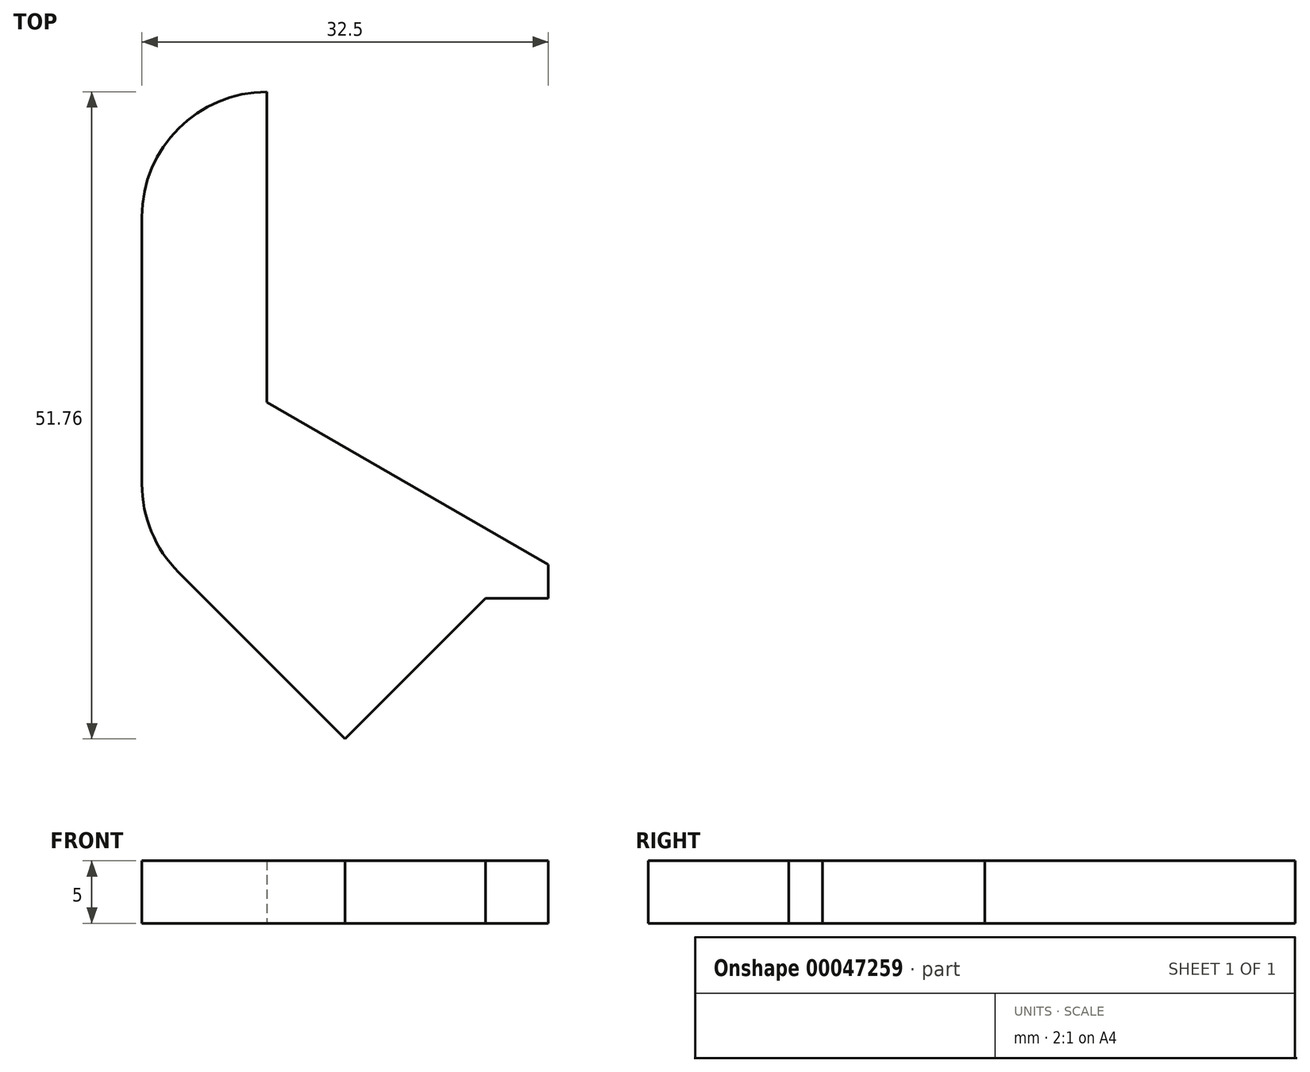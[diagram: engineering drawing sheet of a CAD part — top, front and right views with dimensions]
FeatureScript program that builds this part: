
annotation { "Feature Type Name" : "Feature", "Feature Type Description" : "" }
export const myFeature = defineFeature(function(context is Context, id is Id, definition is map)
    precondition{}
    {
        {
            var Q0;
            Q0=qCreatedBy(makeId("Top.planeOp"),FACE);
            var sketch = newSketch(context, id + "F0", { "sketchPlane" : qUnion([Q0])});
            skCircle(sketch, "E0.cCircle", {"center": v(0, 0) * mm, "radius": 22.5 * mm, "construction": true});
            skLineSegment(sketch, "E0.2", {"start": v(0, -25.98) * mm, "end": v(-22.5, -13) * mm});
            skLineSegment(sketch, "E0.3", {"start": v(-22.5, -13) * mm, "end": v(-22.5, 11.84) * mm});
            skPoint(sketch, "E0.0.midPoint", {"position": v(22.5, 0) * mm});
            skLineSegment(sketch, "E1", {"start": v(-22.5, 11.84) * mm, "end": v(-32.5, 11.84) * mm});
            skLineSegment(sketch, "E2", {"start": v(0, -28.67) * mm, "end": v(-5, -28.67) * mm});
            skLineSegment(sketch, "E3", {"start": v(-5, -28.67) * mm, "end": v(-5, -38.67) * mm});
            skLineSegment(sketch, "E4", {"start": v(-5, -38.67) * mm, "end": v(0, -38.67) * mm});
            skPoint(sketch, "E5.endSnap0", {"position": v(-2, -38.67) * mm});
            skLineSegment(sketch, "E6", {"start": v(-32.5, 11.84) * mm, "end": v(-32.5, -43.67) * mm});
            skPoint(sketch, "E7.MirrorP", {"position": v(0, -38.67) * mm});
            skLineSegment(sketch, "E8.MirrorCS", {"start": v(0, -28.67) * mm, "end": v(5, -28.67) * mm});
            skLineSegment(sketch, "E9.MirrorCS", {"start": v(5, -28.67) * mm, "end": v(5, -38.67) * mm});
            skLineSegment(sketch, "E10.MirrorCS", {"start": v(5, -38.67) * mm, "end": v(0, -38.67) * mm});
            skLineSegment(sketch, "E11", {"start": v(-32.5, -43.67) * mm, "end": v(0, -43.67) * mm});
            skLineSegment(sketch, "E12", {"start": v(0, -43.67) * mm, "end": v(0, -25.98) * mm});
            skLineSegment(sketch, "E13.MirrorCS", {"start": v(22.5, 11.84) * mm, "end": v(32.5, 11.84) * mm});
            skPoint(sketch, "E14.MirrorP", {"position": v(2, -38.67) * mm});
            skCircle(sketch, "E15.MirrorC", {"center": v(0, 0) * mm, "radius": 22.5 * mm});
            skLineSegment(sketch, "E16.MirrorCS", {"start": v(22.5, -13) * mm, "end": v(22.5, 11.84) * mm});
            skLineSegment(sketch, "E17.MirrorCS", {"start": v(32.5, 11.84) * mm, "end": v(32.5, -43.67) * mm});
            skLineSegment(sketch, "E18.MirrorCS", {"start": v(32.5, -43.67) * mm, "end": v(0, -43.67) * mm});
            skLineSegment(sketch, "E19.MirrorCS", {"start": v(0, -25.98) * mm, "end": v(22.5, -13) * mm});
            skPoint(sketch, "E20.MirrorP", {"position": v(-22.5, 0) * mm});
            skSolve(sketch);
        }
        {
            var Q0;
            Q0=makeQuery(id+"F0.imprint","IMPRINT",FACE,{"disambiguationData":[TD([[makeQuery(id+"F0.imprint","IMPRINT",EDGE,{"derivedFrom":sQuery(id+"F0.wireOp",EDGE,"E0.2")}),1.0]])]});
            var Q1;
            {var subQ8=sQuery(id+"F0.wireOp",EDGE,"E8.MirrorCS");Q1=makeQuery(id+"F0.imprint","IMPRINT",FACE,{"disambiguationData":[TD([[makeQuery(id+"F0.imprint","IMPRINT",EDGE,{"derivedFrom":subQ8}),1.0]])]});}
            extrude(context, id + "F1", {"entities" : qUnion([Q0, Q1]), "depth" : 5 * mm});
        }
        {
            var Q0;
            Q0=makeQuery(id+"F1.opExtrude","SWEPT_EDGE",EDGE,{"disambiguationData":[OSD([sQuery(id+"F0.wireOp",EDGE,"E6"),sQuery(id+"F0.wireOp",EDGE,"E11")])]});
            var Q1;
            Q1=makeQuery(id+"F1.opExtrude","SWEPT_EDGE",EDGE,{"disambiguationData":[OSD([sQuery(id+"F0.wireOp",EDGE,"E17.MirrorCS"),sQuery(id+"F0.wireOp",EDGE,"E18.MirrorCS")])]});
            chamfer(context, id + "F2", {"entities" : qUnion([Q0, Q1]), "width" : 20 * mm, "tangentPropagation" : true});
        }
        {
            var Q0;
            {var subQ0=sQuery(id+"F0.wireOp",EDGE,"E6");Q0=makeQuery(id+"F2.opChamfer","BLEND_EDGE",EDGE,{"blendedFrom":[makeQuery(id+"F1.opExtrude","SWEPT_EDGE",EDGE,{"disambiguationData":[OSD([subQ0,sQuery(id+"F0.wireOp",EDGE,"85b966ba-6e7b-4b01-9989-d382e7c03624")])]}),makeQuery(id+"F1.opExtrude","SWEPT_FACE",FACE,{"disambiguationData":[OSD([subQ0])]})],"blendedInto":[makeQuery(id+"F1.opExtrude","SWEPT_FACE",FACE,{"disambiguationData":[OSD([subQ0])]})]});}
            var Q1;
            Q1=makeQuery(id+"F1.opExtrude","SWEPT_EDGE",EDGE,{"disambiguationData":[OSD([sQuery(id+"F0.wireOp",EDGE,"E1"),sQuery(id+"F0.wireOp",EDGE,"E6")])]});
            var Q2;
            Q2=makeQuery(id+"F1.opExtrude","SWEPT_EDGE",EDGE,{"disambiguationData":[OSD([sQuery(id+"F0.wireOp",EDGE,"bf1954ff-a6e5-4024-aeca-9bebb4eaad302.MirrorCS"),sQuery(id+"F0.wireOp",EDGE,"bf1954ff-a6e5-4024-aeca-9bebb4eaad308.MirrorCS")])]});
            var Q3;
            {var subQ0=sQuery(id+"F0.wireOp",EDGE,"bf1954ff-a6e5-4024-aeca-9bebb4eaad308.MirrorCS");Q3=makeQuery(id+"F2.opChamfer","BLEND_EDGE",EDGE,{"blendedFrom":[makeQuery(id+"F1.opExtrude","SWEPT_EDGE",EDGE,{"disambiguationData":[OSD([subQ0,sQuery(id+"F0.wireOp",EDGE,"bf1954ff-a6e5-4024-aeca-9bebb4eaad309.MirrorCS")])]}),makeQuery(id+"F1.opExtrude","SWEPT_FACE",FACE,{"disambiguationData":[OSD([subQ0])]})],"blendedInto":[makeQuery(id+"F1.opExtrude","SWEPT_FACE",FACE,{"disambiguationData":[OSD([subQ0])]})]});}
            var Q4;
            {var subQ0=sQuery(id+"F0.wireOp",EDGE,"bf1954ff-a6e5-4024-aeca-9bebb4eaad309.MirrorCS");Q4=makeQuery(id+"F2.opChamfer","BLEND_EDGE",EDGE,{"blendedFrom":[makeQuery(id+"F1.opExtrude","SWEPT_EDGE",EDGE,{"disambiguationData":[OSD([sQuery(id+"F0.wireOp",EDGE,"bf1954ff-a6e5-4024-aeca-9bebb4eaad308.MirrorCS"),subQ0])]}),makeQuery(id+"F1.opExtrude","SWEPT_FACE",FACE,{"disambiguationData":[OSD([sQuery(id+"F0.wireOp",EDGE,"85b966ba-6e7b-4b01-9989-d382e7c03624"),subQ0])]})],"blendedInto":[makeQuery(id+"F1.opExtrude","SWEPT_FACE",FACE,{"disambiguationData":[OSD([sQuery(id+"F0.wireOp",EDGE,"85b966ba-6e7b-4b01-9989-d382e7c03624"),subQ0])]})]});}
            var Q5;
            {var subQ0=sQuery(id+"F0.wireOp",EDGE,"85b966ba-6e7b-4b01-9989-d382e7c03624");Q5=makeQuery(id+"F2.opChamfer","BLEND_EDGE",EDGE,{"blendedFrom":[makeQuery(id+"F1.opExtrude","SWEPT_EDGE",EDGE,{"disambiguationData":[OSD([sQuery(id+"F0.wireOp",EDGE,"E6"),subQ0])]}),makeQuery(id+"F1.opExtrude","SWEPT_FACE",FACE,{"disambiguationData":[OSD([subQ0,sQuery(id+"F0.wireOp",EDGE,"bf1954ff-a6e5-4024-aeca-9bebb4eaad309.MirrorCS")])]})],"blendedInto":[makeQuery(id+"F1.opExtrude","SWEPT_FACE",FACE,{"disambiguationData":[OSD([subQ0,sQuery(id+"F0.wireOp",EDGE,"bf1954ff-a6e5-4024-aeca-9bebb4eaad309.MirrorCS")])]})]});}
            var Q6;
            {var subQ0=sQuery(id+"F0.wireOp",EDGE,"E17.MirrorCS");Q6=makeQuery(id+"F2.opChamfer","BLEND_EDGE",EDGE,{"blendedFrom":[makeQuery(id+"F1.opExtrude","SWEPT_EDGE",EDGE,{"disambiguationData":[OSD([subQ0,sQuery(id+"F0.wireOp",EDGE,"E18.MirrorCS")])]}),makeQuery(id+"F1.opExtrude","SWEPT_FACE",FACE,{"disambiguationData":[OSD([subQ0])]})],"blendedInto":[makeQuery(id+"F1.opExtrude","SWEPT_FACE",FACE,{"disambiguationData":[OSD([subQ0])]})]});}
            var Q7;
            Q7=makeQuery(id+"F1.opExtrude","SWEPT_EDGE",EDGE,{"disambiguationData":[OSD([sQuery(id+"F0.wireOp",EDGE,"E13.MirrorCS"),sQuery(id+"F0.wireOp",EDGE,"E17.MirrorCS")])]});
            var Q8;
            {var subQ0=sQuery(id+"F0.wireOp",EDGE,"E18.MirrorCS");Q8=makeQuery(id+"F2.opChamfer","BLEND_EDGE",EDGE,{"blendedFrom":[makeQuery(id+"F1.opExtrude","SWEPT_EDGE",EDGE,{"disambiguationData":[OSD([sQuery(id+"F0.wireOp",EDGE,"E17.MirrorCS"),subQ0])]}),makeQuery(id+"F1.opExtrude","SWEPT_FACE",FACE,{"disambiguationData":[OSD([sQuery(id+"F0.wireOp",EDGE,"E11"),subQ0])]})],"blendedInto":[makeQuery(id+"F1.opExtrude","SWEPT_FACE",FACE,{"disambiguationData":[OSD([sQuery(id+"F0.wireOp",EDGE,"E11"),subQ0])]})]});}
            var Q9;
            {var subQ0=sQuery(id+"F0.wireOp",EDGE,"E11");Q9=makeQuery(id+"F2.opChamfer","BLEND_EDGE",EDGE,{"blendedFrom":[makeQuery(id+"F1.opExtrude","SWEPT_EDGE",EDGE,{"disambiguationData":[OSD([sQuery(id+"F0.wireOp",EDGE,"E6"),subQ0])]}),makeQuery(id+"F1.opExtrude","SWEPT_FACE",FACE,{"disambiguationData":[OSD([subQ0,sQuery(id+"F0.wireOp",EDGE,"E18.MirrorCS")])]})],"blendedInto":[makeQuery(id+"F1.opExtrude","SWEPT_FACE",FACE,{"disambiguationData":[OSD([subQ0,sQuery(id+"F0.wireOp",EDGE,"E18.MirrorCS")])]})]});}
            fillet(context, id + "F3", {"entities" : qUnion([Q0, Q1, Q2, Q3, Q4, Q5, Q6, Q7, Q8, Q9]), "radius" : 10 * mm, "tangentPropagation" : true, "allowEdgeOverflow" : false});
        }
    });
